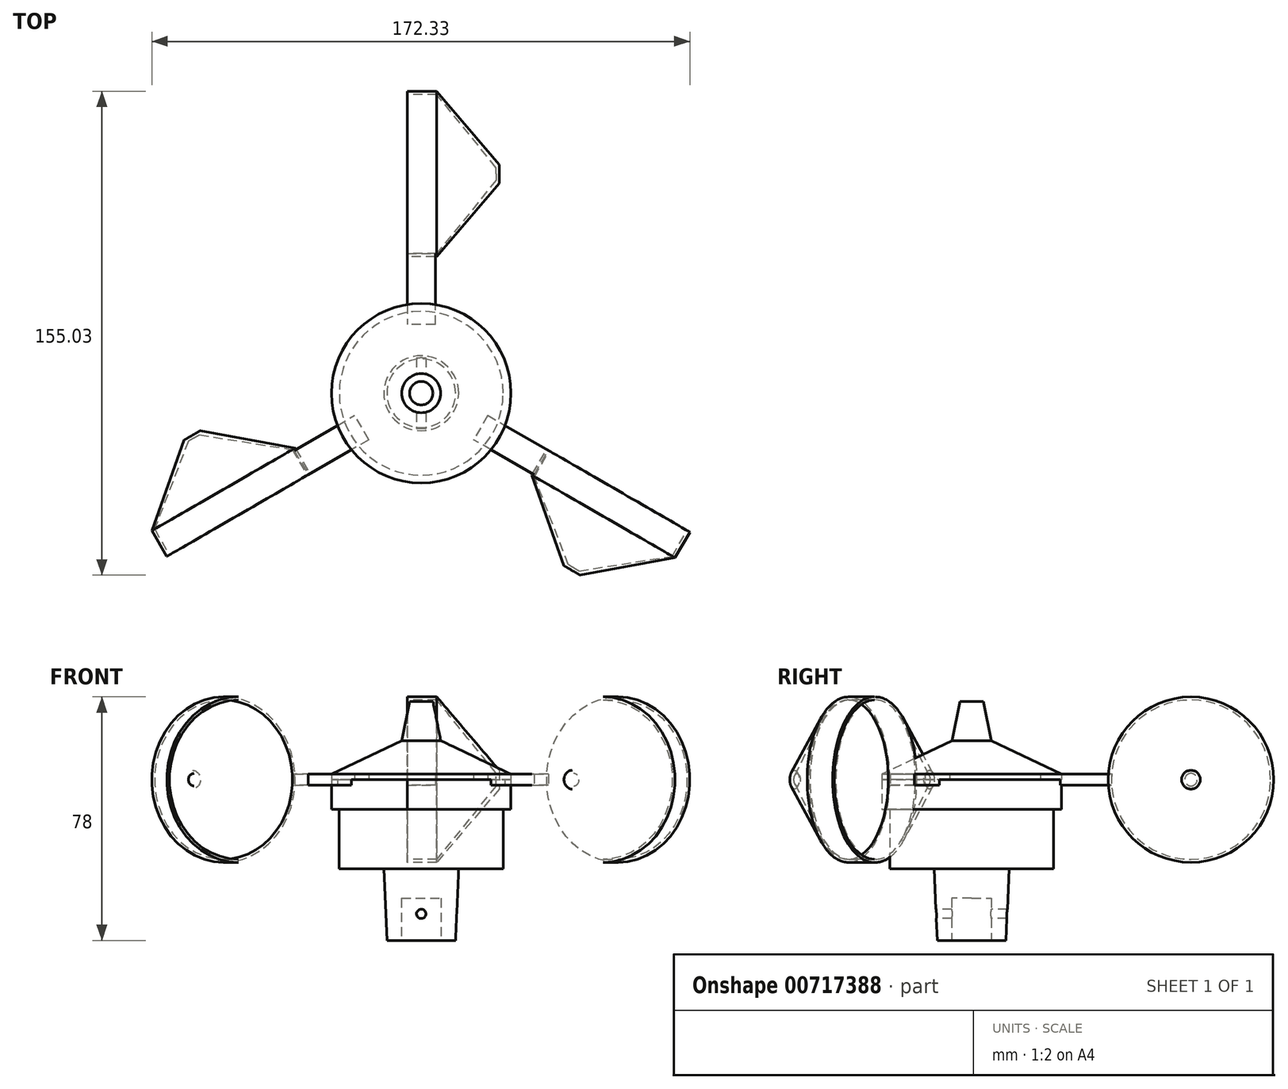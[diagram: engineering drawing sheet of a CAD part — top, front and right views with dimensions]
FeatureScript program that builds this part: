
annotation { "Feature Type Name" : "Feature", "Feature Type Description" : "" }
export const myFeature = defineFeature(function(context is Context, id is Id, definition is map)
    precondition{}
    {
        {
            var Q0;
            Q0=qCreatedBy(makeId("Top.planeOp"),FACE);
            var sketch = newSketch(context, id + "F0", { "sketchPlane" : qUnion([Q0])});
            skCircle(sketch, "E0", {"center": v(0, 0) * mm, "radius": 11 * mm});
            skSolve(sketch);
        }
        {
            var Q0;
            Q0=qCreatedBy(makeId("Top.planeOp"),FACE);
            cPlane(context, id + "F1", {"entities" : qUnion([Q0]), "cplaneType" : CPlaneType.OFFSET, "offset" : 23 * mm, "width" : 150 * mm, "height" : 150 * mm});
        }
        {
            var Q0;
            Q0=qCreatedBy(id+"F1.planeOp",FACE);
            var sketch = newSketch(context, id + "F2", { "sketchPlane" : qUnion([Q0])});
            skCircle(sketch, "E1", {"center": v(0, 0) * mm, "radius": 12 * mm});
            skSolve(sketch);
        }
        {
            var Q0;
            Q0=makeQuery(id+"F0.imprint","IMPRINT",FACE,{"disambiguationData":[TD([[makeQuery(id+"F0.imprint","IMPRINT",EDGE,{"derivedFrom":sQuery(id+"F0.wireOp",EDGE,"E0")}),1.0]])]});
            var Q1;
            Q1=makeQuery(id+"F2.imprint","IMPRINT",FACE,{"disambiguationData":[TD([[makeQuery(id+"F2.imprint","IMPRINT",EDGE,{"derivedFrom":sQuery(id+"F2.wireOp",EDGE,"E1")}),1.0]])]});
            loft(context, id + "F3", {"sheetProfilesArray" : [{ "sheetProfileEntities" : qUnion([Q0]) }, { "sheetProfileEntities" : qUnion([Q1]) }]});
        }
        {
            var Q0;
            Q0=makeQuery(id+"F3.opLoft","CAP_FACE",FACE,{"disambiguationData":[OSD([makeQuery(id+"F0.imprint","IMPRINT",FACE,{"disambiguationData":[TD([[makeQuery(id+"F0.imprint","IMPRINT",EDGE,{"derivedFrom":sQuery(id+"F0.wireOp",EDGE,"E0")}),1.0]])]})])],"isStart":true});
            var sketch = newSketch(context, id + "F4", { "sketchPlane" : qUnion([Q0])});
            skCircle(sketch, "E2.0", {"center": v(0, 0) * mm, "radius": 6.35 * mm});
            skSolve(sketch);
        }
        {
            var Q0;
            Q0=makeQuery(id+"F3.opLoft","CAP_FACE",FACE,{"disambiguationData":[OSD([makeQuery(id+"F2.imprint","IMPRINT",FACE,{"disambiguationData":[TD([[makeQuery(id+"F2.imprint","IMPRINT",EDGE,{"derivedFrom":sQuery(id+"F2.wireOp",EDGE,"E1")}),1.0]])]})])],"isStart":true});
            var sketch = newSketch(context, id + "F5", { "sketchPlane" : qUnion([Q0])});
            skCircle(sketch, "E3.0", {"center": v(0, 0) * mm, "radius": 6.35 * mm});
            skSolve(sketch);
        }
        {
            var Q1;
            Q1=makeQuery(id+"F4.imprint","IMPRINT",FACE,{"disambiguationData":[TD([[makeQuery(id+"F4.imprint","IMPRINT",EDGE,{"derivedFrom":sQuery(id+"F4.wireOp",EDGE,"E2.0")}),1.0]])]});
            var Q2;
            Q2=makeQuery(id+"F5.imprint","IMPRINT",FACE,{"disambiguationData":[TD([[makeQuery(id+"F5.imprint","IMPRINT",EDGE,{"derivedFrom":sQuery(id+"F5.wireOp",EDGE,"E3.0")}),1.0]])]});
            loft(context, id + "F6", {"operationType" : NewBodyOperationType.REMOVE, "sheetProfilesArray" : [{ "sheetProfileEntities" : qUnion([Q1]) }, { "sheetProfileEntities" : qUnion([Q2]) }]});
        }
        {
            var Q0;
            Q0=makeQuery(id+"F3.opLoft","CAP_FACE",FACE,{"disambiguationData":[OSD([makeQuery(id+"F2.imprint","IMPRINT",FACE,{"disambiguationData":[TD([[makeQuery(id+"F2.imprint","IMPRINT",EDGE,{"derivedFrom":sQuery(id+"F2.wireOp",EDGE,"E1")}),1.0]])]})])],"isStart":true});
            var sketch = newSketch(context, id + "F7", { "sketchPlane" : qUnion([Q0])});
            skCircle(sketch, "E4", {"center": v(0, 0) * mm, "radius": 26.25 * mm});
            skSolve(sketch);
        }
        {
            var Q0;
            Q0=qSketchRegion(id+"F7",true);
            extrude(context, id + "F8", {"entities" : qUnion([Q0]), "operationType" : NewBodyOperationType.ADD, "depth" : 19 * mm, "offsetDistance" : 25 * mm});
        }
        {
            var Q0;
            Q0=makeQuery(id+"F8.opExtrude","CAP_FACE",FACE,{"disambiguationData":[OSD([sQuery(id+"F7.wireOp",EDGE,"E4")])],"isStart":false});
            var sketch = newSketch(context, id + "F9", { "sketchPlane" : qUnion([Q0])});
            skCircle(sketch, "E5", {"center": v(0, 0) * mm, "radius": 28.75 * mm});
            skSolve(sketch);
        }
        {
            var Q0;
            Q0=qSketchRegion(id+"F9",true);
            extrude(context, id + "F10", {"entities" : qUnion([Q0]), "operationType" : NewBodyOperationType.ADD, "depth" : 9.5 * mm, "offsetDistance" : 25 * mm});
        }
        {
            var Q0;
            Q0=qCreatedBy(id+"F1.planeOp",FACE);
            var sketch = newSketch(context, id + "F11", { "sketchPlane" : qUnion([Q0])});
            skLineSegment(sketch, "E6", {"start": v(-4.5, 28.4) * mm, "end": v(-4.5, 44.75) * mm});
            skLineSegment(sketch, "E7", {"start": v(-4.5, 44.75) * mm, "end": v(0, 44.75) * mm});
            skLineSegment(sketch, "E8", {"start": v(0, 44.75) * mm, "end": v(4.5, 44.75) * mm});
            skLineSegment(sketch, "E9", {"start": v(4.5, 44.75) * mm, "end": v(4.5, 28.4) * mm});
            skLineSegment(sketch, "E10", {"start": v(0, 0) * mm, "end": v(-51.38, -29.67) * mm, "construction": true});
            skLineSegment(sketch, "E11", {"start": v(0, 0) * mm, "end": v(61.77, -35.66) * mm, "construction": true});
            skArc(sketch, "E12.0", {"start": v(4.5, 28.4) * mm, "mid": v(0, 28.75) * mm, "end": v(-4.5, 28.4) * mm});
            skLineSegment(sketch, "E13", {"start": v(-26.84, -10.3) * mm, "end": v(-40.7, -18.3) * mm});
            skLineSegment(sketch, "E14", {"start": v(-40.7, -18.3) * mm, "end": v(-36.2, -26.1) * mm});
            skLineSegment(sketch, "E15", {"start": v(-36.2, -26.1) * mm, "end": v(-22.34, -18.1) * mm});
            skLineSegment(sketch, "E16", {"start": v(22.34, -18.1) * mm, "end": v(36.2, -26.1) * mm});
            skLineSegment(sketch, "E17", {"start": v(36.2, -26.1) * mm, "end": v(40.7, -18.3) * mm});
            skLineSegment(sketch, "E18", {"start": v(40.7, -18.3) * mm, "end": v(26.84, -10.3) * mm});
            skArc(sketch, "E19.trimOffspring", {"start": v(-26.84, -10.3) * mm, "mid": v(-24.9, -14.38) * mm, "end": v(-22.34, -18.1) * mm});
            skArc(sketch, "E20.trimOffspring", {"start": v(22.34, -18.1) * mm, "mid": v(24.9, -14.37) * mm, "end": v(26.84, -10.3) * mm});
            skSolve(sketch);
        }
        {
            var Q0;
            Q0=makeQuery(id+"F10.opExtrude","CAP_FACE",FACE,{"disambiguationData":[OSD([sQuery(id+"F9.wireOp",EDGE,"E5")])],"isStart":false});
            var sketch = newSketch(context, id + "F12", { "sketchPlane" : qUnion([Q0])});
            skLineSegment(sketch, "E21.0", {"start": v(-4.5, 28.4) * mm, "end": v(-4.5, 44.75) * mm});
            skLineSegment(sketch, "E21.1", {"start": v(-4.5, 44.75) * mm, "end": v(0, 44.75) * mm});
            skLineSegment(sketch, "E21.2", {"start": v(0, 44.75) * mm, "end": v(4.5, 44.75) * mm});
            skLineSegment(sketch, "E21.3", {"start": v(4.5, 44.75) * mm, "end": v(4.5, 28.4) * mm});
            skLineSegment(sketch, "E21.4", {"start": v(0, 0) * mm, "end": v(-51.38, -29.67) * mm, "construction": true});
            skLineSegment(sketch, "E21.5", {"start": v(0, 0) * mm, "end": v(61.77, -35.66) * mm, "construction": true});
            skLineSegment(sketch, "E21.7", {"start": v(-26.84, -10.3) * mm, "end": v(-40.7, -18.3) * mm});
            skLineSegment(sketch, "E21.8", {"start": v(-40.7, -18.3) * mm, "end": v(-36.2, -26.1) * mm});
            skLineSegment(sketch, "E21.9", {"start": v(-36.2, -26.1) * mm, "end": v(-22.34, -18.1) * mm});
            skLineSegment(sketch, "E21.10", {"start": v(22.34, -18.1) * mm, "end": v(36.2, -26.1) * mm});
            skLineSegment(sketch, "E21.11", {"start": v(36.2, -26.1) * mm, "end": v(40.7, -18.3) * mm});
            skLineSegment(sketch, "E21.12", {"start": v(40.7, -18.3) * mm, "end": v(26.84, -10.3) * mm});
            skLineSegment(sketch, "E22", {"start": v(0, 0) * mm, "end": v(0, 55.38) * mm, "construction": true});
            skLineSegment(sketch, "E23", {"start": v(-26.84, -10.3) * mm, "end": v(-21.3, -7.1) * mm});
            skLineSegment(sketch, "E24", {"start": v(-21.3, -7.1) * mm, "end": v(-16.8, -14.9) * mm});
            skLineSegment(sketch, "E25", {"start": v(-16.8, -14.9) * mm, "end": v(-22.34, -18.1) * mm});
            skLineSegment(sketch, "E26", {"start": v(22.34, -18.1) * mm, "end": v(16.8, -14.9) * mm});
            skLineSegment(sketch, "E27", {"start": v(16.8, -14.9) * mm, "end": v(21.3, -7.1) * mm});
            skLineSegment(sketch, "E28", {"start": v(21.3, -7.1) * mm, "end": v(26.84, -10.3) * mm});
            skLineSegment(sketch, "E29", {"start": v(-4.5, 28.4) * mm, "end": v(-4.5, 22) * mm});
            skLineSegment(sketch, "E30", {"start": v(-4.5, 22) * mm, "end": v(4.5, 22) * mm});
            skLineSegment(sketch, "E31", {"start": v(4.5, 22) * mm, "end": v(4.5, 28.4) * mm});
            skPoint(sketch, "E21.13.start.orphan", {"position": v(-26.84, -10.3) * mm});
            skPoint(sketch, "E32.orphan", {"position": v(22.34, -18.1) * mm});
            skPoint(sketch, "E21.14.end.orphan", {"position": v(26.84, -10.3) * mm});
            skPoint(sketch, "E33.orphan", {"position": v(-4.5, 28.4) * mm});
            skSolve(sketch);
        }
        {
            var Q0;
            Q0=qSketchRegion(id+"F12",true);
            extrude(context, id + "F13", {"entities" : qUnion([Q0]), "operationType" : NewBodyOperationType.ADD, "endBound" : BoundingType.SYMMETRIC, "depth" : 3.5 * mm, "offsetDistance" : 25 * mm});
        }
        {
            var Q0;
            Q0=makeQuery(id+"F10.opExtrude","CAP_FACE",FACE,{"disambiguationData":[OSD([sQuery(id+"F9.wireOp",EDGE,"E5")])],"isStart":false});
            cPlane(context, id + "F14", {"entities" : qUnion([Q0]), "cplaneType" : CPlaneType.OFFSET, "offset" : 12.5 * mm, "width" : 150 * mm, "height" : 150 * mm});
        }
        {
            var Q0;
            Q0=makeQuery(id+"F10.opExtrude","CAP_FACE",FACE,{"disambiguationData":[OSD([sQuery(id+"F9.wireOp",EDGE,"E5")])],"isStart":false});
            var sketch = newSketch(context, id + "F15", { "sketchPlane" : qUnion([Q0])});
            skCircle(sketch, "E34", {"center": v(0, 0) * mm, "radius": 28.75 * mm});
            skSolve(sketch);
        }
        {
            var Q0;
            Q0=qCreatedBy(id+"F14.planeOp",FACE);
            var sketch = newSketch(context, id + "F16", { "sketchPlane" : qUnion([Q0])});
            skCircle(sketch, "E35", {"center": v(0, 0) * mm, "radius": 6.25 * mm});
            skSolve(sketch);
        }
        {
            var Q0;
            Q0=qSketchRegion(id+"F15",true);
            extrude(context, id + "F17", {"entities" : qUnion([Q0]), "depth" : 3.5 / 2 * mm, "offsetDistance" : 25 * mm});
        }
        {
            var Q0;
            Q0=makeQuery(id+"F17.opExtrude","CAP_FACE",FACE,{"disambiguationData":[OSD([sQuery(id+"F15.wireOp",EDGE,"E34")])],"isStart":false});
            var Q1;
            Q1=makeQuery(id+"F16.imprint","IMPRINT",FACE,{"disambiguationData":[TD([[makeQuery(id+"F16.imprint","IMPRINT",EDGE,{"derivedFrom":sQuery(id+"F16.wireOp",EDGE,"E35")}),1.0]])]});
            loft(context, id + "F18", {"sheetProfilesArray" : [{ "sheetProfileEntities" : qUnion([Q0]) }, { "sheetProfileEntities" : qUnion([Q1]) }]});
        }
        {
            var Q0;
            Q0=makeQuery(id+"F18.opLoft","CAP_FACE",FACE,{"disambiguationData":[OSD([makeQuery(id+"F16.imprint","IMPRINT",FACE,{"disambiguationData":[TD([[makeQuery(id+"F16.imprint","IMPRINT",EDGE,{"derivedFrom":sQuery(id+"F16.wireOp",EDGE,"E35")}),1.0]])]})])],"isStart":true});
            var sketch = newSketch(context, id + "F19", { "sketchPlane" : qUnion([Q0])});
            skCircle(sketch, "E36.0", {"center": v(0, 0) * mm, "radius": 6.25 * mm});
            skSolve(sketch);
        }
        {
            var Q0;
            Q0=makeQuery(id+"F19.imprint","IMPRINT",FACE,{"disambiguationData":[TD([[makeQuery(id+"F19.imprint","IMPRINT",EDGE,{"derivedFrom":sQuery(id+"F19.wireOp",EDGE,"E36.0")}),1.0]])]});
            cPlane(context, id + "F20", {"entities" : qUnion([Q0]), "cplaneType" : CPlaneType.OFFSET, "offset" : 12.5 * mm, "width" : 150 * mm, "height" : 150 * mm});
        }
        {
            var Q0;
            Q0=qCreatedBy(id+"F20.planeOp",FACE);
            var sketch = newSketch(context, id + "F21", { "sketchPlane" : qUnion([Q0])});
            skCircle(sketch, "E37", {"center": v(0, 0) * mm, "radius": 3.75 * mm});
            skSolve(sketch);
        }
        {
            var Q1;
            Q1=makeQuery(id+"F19.imprint","IMPRINT",FACE,{"disambiguationData":[TD([[makeQuery(id+"F19.imprint","IMPRINT",EDGE,{"derivedFrom":sQuery(id+"F19.wireOp",EDGE,"E36.0")}),1.0]])]});
            var Q2;
            Q2=makeQuery(id+"F21.imprint","IMPRINT",FACE,{"disambiguationData":[TD([[makeQuery(id+"F21.imprint","IMPRINT",EDGE,{"derivedFrom":sQuery(id+"F21.wireOp",EDGE,"E37")}),1.0]])]});
            loft(context, id + "F22", {"operationType" : NewBodyOperationType.ADD, "sheetProfilesArray" : [{ "sheetProfileEntities" : qUnion([Q1]) }, { "sheetProfileEntities" : qUnion([Q2]) }]});
        }
        {
            var Q0;
            Q0=makeQuery(id+"F13.opExtrude","SWEPT_FACE",FACE,{"disambiguationData":[OSD([sQuery(id+"F12.wireOp",EDGE,"E21.0"),sQuery(id+"F12.wireOp",EDGE,"E29")])]});
            var sketch = newSketch(context, id + "F23", { "sketchPlane" : qUnion([Q0])});
            skCircle(sketch, "E38", {"center": v(-70.25, 51.5) * mm, "radius": 25.5 * mm});
            skPoint(sketch, "E38.centerSnap0", {"position": v(-44.75, 51.5) * mm});
            skCircle(sketch, "E39.0", {"center": v(-70.25, 51.5) * mm, "radius": 26.5 * mm});
            skSolve(sketch);
        }
        {
            var Q0;
            Q0=qSketchRegion(id+"F23",true);
            extrude(context, id + "F24", {"entities" : qUnion([Q0]), "oppositeDirection" : true, "depth" : 9.5 * mm, "offsetDistance" : 25 * mm});
        }
        {
            var Q0;
            Q0=makeQuery(id+"F24.opExtrude","CAP_FACE",FACE,{"disambiguationData":[OSD([sQuery(id+"F23.wireOp",EDGE,"E38"),sQuery(id+"F23.wireOp",EDGE,"E39.0")])],"isStart":false});
            cPlane(context, id + "F25", {"entities" : qUnion([Q0]), "cplaneType" : CPlaneType.OFFSET, "offset" : 20 * mm, "width" : 150 * mm, "height" : 150 * mm});
        }
        {
            var Q0;
            Q0=qCreatedBy(id+"F25.planeOp",FACE);
            var sketch = newSketch(context, id + "F26", { "sketchPlane" : qUnion([Q0])});
            skCircle(sketch, "E40", {"center": v(70.25, 51.5) * mm, "radius": 3 * mm});
            skSolve(sketch);
        }
        {
            var Q0;
            Q0=makeQuery(id+"F24.opExtrude","CAP_FACE",FACE,{"disambiguationData":[OSD([sQuery(id+"F23.wireOp",EDGE,"E38"),sQuery(id+"F23.wireOp",EDGE,"E39.0")])],"isStart":false});
            var sketch = newSketch(context, id + "F27", { "sketchPlane" : qUnion([Q0])});
            skCircle(sketch, "E41.0", {"center": v(70.25, 51.5) * mm, "radius": 26.5 * mm});
            skSolve(sketch);
        }
        {
            var Q1;
            Q1=qSketchRegion(id+"F27",true);
            var Q2;
            Q2=qSketchRegion(id+"F26",true);
            loft(context, id + "F28", {"operationType" : NewBodyOperationType.ADD, "sheetProfilesArray" : [{ "sheetProfileEntities" : qUnion([Q1]) }, { "sheetProfileEntities" : qUnion([Q2]) }]});
        }
        {
            var Q0;
            Q0=qCreatedBy(id+"F25.planeOp",FACE);
            cPlane(context, id + "F29", {"entities" : qUnion([Q0]), "cplaneType" : CPlaneType.OFFSET, "offset" : 1 * mm, "oppositeDirection" : true, "width" : 150 * mm, "height" : 150 * mm});
        }
        {
            var Q0;
            Q0=qCreatedBy(id+"F29.planeOp",FACE);
            var sketch = newSketch(context, id + "F30", { "sketchPlane" : qUnion([Q0])});
            skCircle(sketch, "E42.0", {"center": v(70.25, 51.5) * mm, "radius": 2 * mm});
            skSolve(sketch);
        }
        {
            var Q0;
            Q0=makeQuery(id+"F28.opLoft","CAP_FACE",FACE,{"disambiguationData":[OSD([makeQuery(id+"F27.imprint","IMPRINT",FACE,{"disambiguationData":[TD([[makeQuery(id+"F27.imprint","IMPRINT",EDGE,{"derivedFrom":makeQuery(id+"F24.opExtrude","CAP_EDGE",EDGE,{"disambiguationData":[OSD([sQuery(id+"F23.wireOp",EDGE,"E38")])],"isStart":false})}),-1.0]])]})])],"isStart":true});
            var sketch = newSketch(context, id + "F31", { "sketchPlane" : qUnion([Q0])});
            skCircle(sketch, "E43.0", {"center": v(-70.25, 51.5) * mm, "radius": 25.5 * mm});
            skSolve(sketch);
        }
        {
            var Q1;
            Q1=qSketchRegion(id+"F30",true);
            var Q2;
            Q2=qSketchRegion(id+"F31",true);
            loft(context, id + "F32", {"operationType" : NewBodyOperationType.REMOVE, "sheetProfilesArray" : [{ "sheetProfileEntities" : qUnion([Q1]) }, { "sheetProfileEntities" : qUnion([Q2]) }]});
        }
        {
            var Q0;
            Q0=qCreatedBy(makeId("Right.planeOp"),FACE);
            var sketch = newSketch(context, id + "F33", { "sketchPlane" : qUnion([Q0])});
            skLineSegment(sketch, "E44", {"start": v(0, 0) * mm, "end": v(0, 81.1) * mm, "construction": true});
            skSolve(sketch);
        }
        {
            var Q0;
            Q0=makeQuery(id+"F24.opExtrude","SWEPT_BODY",BODY,{"disambiguationData":[OSD([sQuery(id+"F23.wireOp",EDGE,"E38"),sQuery(id+"F23.wireOp",EDGE,"E39.0")])]});
            var Q1;
            Q1=makeQuery(id+"F28.opLoft","SWEPT_BODY",BODY,{"disambiguationData":[OSD([makeQuery(id+"F26.imprint","IMPRINT",FACE,{"disambiguationData":[TD([[makeQuery(id+"F26.imprint","IMPRINT",EDGE,{"derivedFrom":sQuery(id+"F26.wireOp",EDGE,"E40")}),1.0]])]}),makeQuery(id+"F27.imprint","IMPRINT",FACE,{"disambiguationData":[TD([[makeQuery(id+"F27.imprint","IMPRINT",EDGE,{"derivedFrom":sQuery(id+"F27.wireOp",EDGE,"E41.0")}),-1.0]])]})])]});
            var Q2;
            Q2=sQuery(id+"F33.wireOp",EDGE,"E44");
            circularPattern(context, id + "F34", {"entities" : qUnion([Q0, Q1]), "axis" : qUnion([Q2]), "angle" : 360 * degree, "instanceCount" : 3, "equalSpace" : true});
        }
        {
            var Q0;
            Q0=qCreatedBy(makeId("Front.planeOp"),FACE);
            var sketch = newSketch(context, id + "F35", { "sketchPlane" : qUnion([Q0])});
            skCircle(sketch, "E45", {"center": v(0, 8.5) * mm, "radius": 1.5 * mm});
            skSolve(sketch);
        }
        {
            var Q0;
            Q0=qSketchRegion(id+"F35",true);
            extrude(context, id + "F36", {"entities" : qUnion([Q0]), "operationType" : NewBodyOperationType.REMOVE, "endBound" : BoundingType.SYMMETRIC, "oppositeDirection" : true, "depth" : 25 * mm, "offsetDistance" : 25 * mm});
        }
        {
            var Q0;
            Q0=makeQuery(id+"F8.boolean.opBoolean","SPLIT",FACE,{"disambiguationData":[TD([makeQuery(id+"F6.boolean.opBoolean","COPY",FACE,{"derivedFrom":makeQuery(id+"F6.opLoft","SWEPT_FACE",FACE,{"disambiguationData":[OSD([sQuery(id+"F4.wireOp",EDGE,"E2.0"),sQuery(id+"F5.wireOp",EDGE,"E3.0")])]})})])],"derivedFrom":makeQuery(id+"F8.opExtrude","CAP_FACE",FACE,{"disambiguationData":[OSD([sQuery(id+"F7.wireOp",EDGE,"E4")])],"isStart":true})});
            var sketch = newSketch(context, id + "F37", { "sketchPlane" : qUnion([Q0])});
            skCircle(sketch, "E46.0", {"center": v(0, 0) * mm, "radius": 6.35 * mm});
            skSolve(sketch);
        }
        {
            var Q0;
            Q0 = qSketchRegion(id + "F37", true);
            extrude(context, id + "F38", {"entities" : qUnion([Q0]), "operationType" : NewBodyOperationType.ADD, "depth" : 9.5 * mm, "offsetDistance" : 25 * mm});
        }
    });
